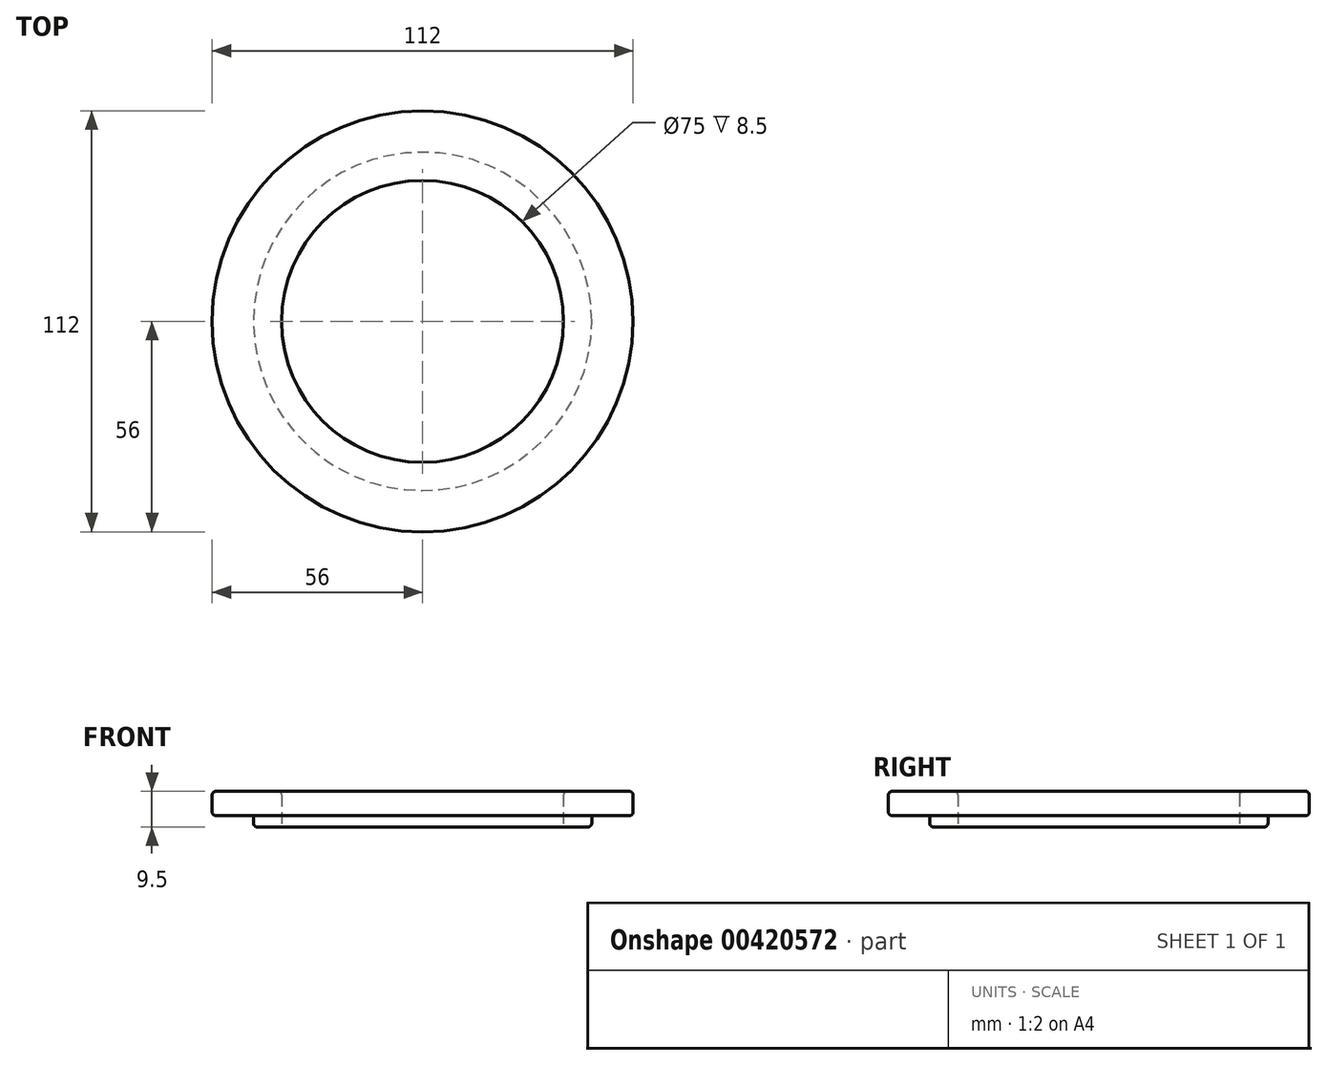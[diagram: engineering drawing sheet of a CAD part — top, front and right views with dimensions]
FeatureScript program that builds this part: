
annotation { "Feature Type Name" : "Feature", "Feature Type Description" : "" }
export const myFeature = defineFeature(function(context is Context, id is Id, definition is map)
    precondition{}
    {
        {
            var Q0;
            Q0=qCreatedBy(makeId("Top.planeOp"),FACE);
            var sketch = newSketch(context, id + "F0", { "sketchPlane" : qUnion([Q0])});
            skCircle(sketch, "E0", {"center": v(0, 0) * mm, "radius": 56 * mm});
            skCircle(sketch, "E1", {"center": v(0, 0) * mm, "radius": 37.5 * mm});
            skSolve(sketch);
        }
        {
            var Q0;
            Q0=makeQuery(id+"F0.imprint","IMPRINT",FACE,{"disambiguationData":[TD([[makeQuery(id+"F0.imprint","IMPRINT",EDGE,{"derivedFrom":sQuery(id+"F0.wireOp",EDGE,"E0")}),-1.0]])]});
            var Q1;
            Q1=makeQuery(id+"F0.imprint","IMPRINT",FACE,{"disambiguationData":[TD([[makeQuery(id+"F0.imprint","IMPRINT",EDGE,{"derivedFrom":sQuery(id+"F0.wireOp",EDGE,"E0")}),1.0]])]});
            extrude(context, id + "F1", {"entities" : qUnion([Q0, Q1]), "offsetDistance" : 25 * mm, "depth" : 6.5 * mm});
        }
        {
            var Q0;
            Q0=qCreatedBy(makeId("Top.planeOp"),FACE);
            var sketch = newSketch(context, id + "F2", { "sketchPlane" : qUnion([Q0])});
            skCircle(sketch, "E2", {"center": v(0, 0) * mm, "radius": 45 * mm});
            skCircle(sketch, "E3", {"center": v(0, 0) * mm, "radius": 37.5 * mm});
            skSolve(sketch);
        }
        {
            var Q0;
            Q0 = qSketchRegion(id + "F2", true);
            extrude(context, id + "F3", {"entities" : qUnion([Q0]), "operationType" : NewBodyOperationType.ADD, "oppositeDirection" : true, "offsetDistance" : 25 * mm, "depth" : 3 * mm});
        }
        {
            var Q0;
            Q0=makeQuery(id+"F3.boolean.opBoolean","INTERSECT",EDGE,{"derivedFrom":[makeQuery(id+"F1.opExtrude","SWEPT_FACE",FACE,{"disambiguationData":[OSD([sQuery(id+"F0.wireOp",EDGE,"E0")])]}),makeQuery(id+"F3.opExtrude","CAP_FACE",FACE,{"disambiguationData":[OSD([sQuery(id+"F2.wireOp",EDGE,"E2"),sQuery(id+"F2.wireOp",EDGE,"E3")])],"isStart":false})]});
            var Q1;
            Q1=makeQuery(id+"F1.opExtrude","CAP_EDGE",EDGE,{"disambiguationData":[OSD([sQuery(id+"F0.wireOp",EDGE,"E0")])],"isStart":false});
            var Q2;
            Q2=makeQuery(id+"F3.opExtrude","CAP_EDGE",EDGE,{"disambiguationData":[OSD([sQuery(id+"F2.wireOp",EDGE,"E2")])],"isStart":false});
            var Q3;
            Q3=makeQuery(id+"F3.opExtrude","CAP_EDGE",EDGE,{"disambiguationData":[OSD([sQuery(id+"F2.wireOp",EDGE,"E2")])],"isStart":true});
            var Q4;
            Q4=makeQuery(id+"F1.opExtrude","CAP_EDGE",EDGE,{"disambiguationData":[OSD([sQuery(id+"F0.wireOp",EDGE,"E1")])],"isStart":true});
            var Q5;
            Q5=makeQuery(id+"F1.opExtrude","CAP_EDGE",EDGE,{"disambiguationData":[OSD([sQuery(id+"F0.wireOp",EDGE,"E1")])],"isStart":false});
            var Q6;
            Q6=makeQuery(id+"F1.opExtrude","CAP_EDGE",EDGE,{"disambiguationData":[OSD([sQuery(id+"F0.wireOp",EDGE,"E0")])],"isStart":true});
            fillet(context, id + "F4", {"entities" : qUnion([Q0, Q1, Q2, Q3, Q4, Q5, Q6]), "radius" : 1 * mm, "tangentPropagation" : true, "defaultsChanged" : false, "vertexSettings" : [], "allowEdgeOverflow" : false});
        }
    });
